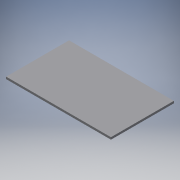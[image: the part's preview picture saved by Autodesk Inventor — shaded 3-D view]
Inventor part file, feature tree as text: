
AUTODESK INVENTOR PART (.ipt)
format: ipt  version: 2016 (Build 200138000, 138)  size: 94,208 bytes
history: native  units: mm
features: extrude x1, sketch x1
ambient origin geometry x8: Origin, YZ Plane, XZ Plane, XY Plane, X Axis, Y Axis, Z Axis, Center Point
bodies: Solid1 (feature_tree)
feature tree (2):
  extrude  "Extrusion1"  [1 undecoded]
  sketch  "Sketch1"  dims[d3=0.0mm]
note: 1 required parameter value undecoded (feature->parameter linkage not recoverable at this tier; creation-order binding heuristic only, values carry confidence <= 0.55)
